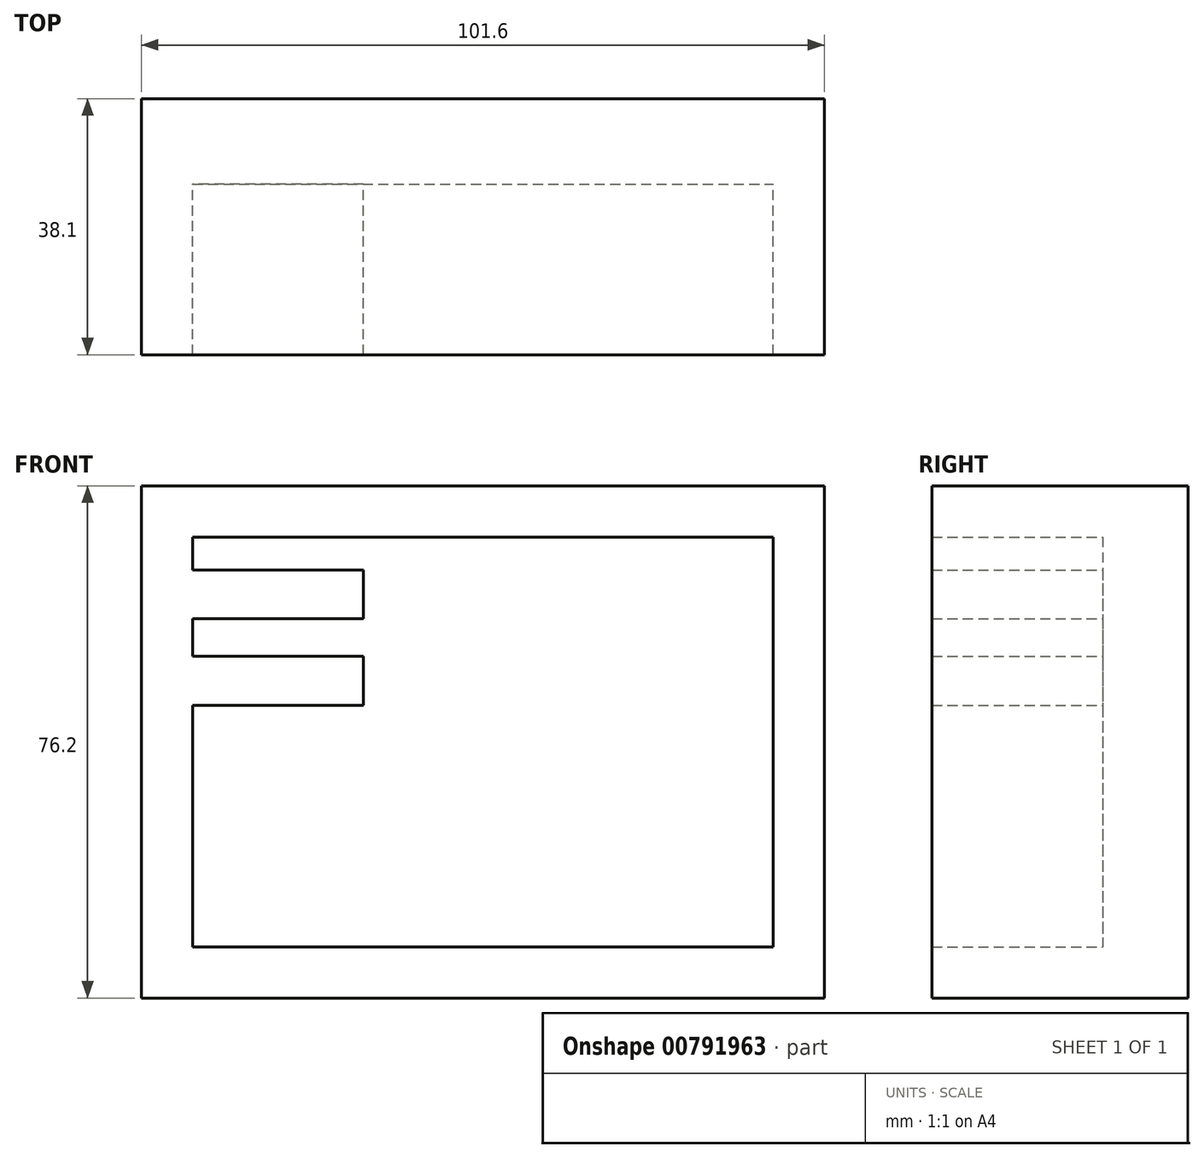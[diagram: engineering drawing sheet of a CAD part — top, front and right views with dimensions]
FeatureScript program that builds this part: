
annotation { "Feature Type Name" : "Feature", "Feature Type Description" : "" }
export const myFeature = defineFeature(function(context is Context, id is Id, definition is map)
    precondition{}
    {
        {
            var Q0;
            Q0=qCreatedBy(makeId("Front.planeOp"),FACE);
            var sketch = newSketch(context, id + "F0", { "sketchPlane" : qUnion([Q0])});
            skLineSegment(sketch, "E0.bottom", {"start": v(-69.79, 37.31) * mm, "end": v(31.81, 37.31) * mm});
            skLineSegment(sketch, "E0.top", {"start": v(-69.79, -38.89) * mm, "end": v(31.81, -38.89) * mm});
            skLineSegment(sketch, "E0.left", {"start": v(-69.79, 37.31) * mm, "end": v(-69.79, -38.89) * mm});
            skLineSegment(sketch, "E0.right", {"start": v(31.81, 37.31) * mm, "end": v(31.81, -38.89) * mm});
            skLineSegment(sketch, "E1.bottom", {"start": v(-62.17, 29.7) * mm, "end": v(24.2, 29.7) * mm});
            skLineSegment(sketch, "E1.top", {"start": v(-62.17, -31.27) * mm, "end": v(24.2, -31.27) * mm});
            skLineSegment(sketch, "E1.left", {"start": v(-62.17, 29.7) * mm, "end": v(-62.17, -31.27) * mm});
            skLineSegment(sketch, "E1.right", {"start": v(24.2, 29.7) * mm, "end": v(24.2, -31.27) * mm});
            skSolve(sketch);
        }
        {
            var Q0;
            Q0=makeQuery(id+"F0.imprint","IMPRINT",FACE,{"disambiguationData":[TD([[makeQuery(id+"F0.imprint","IMPRINT",EDGE,{"derivedFrom":sQuery(id+"F0.wireOp",EDGE,"E0.bottom")}),-1.0]])]});
            extrude(context, id + "F1", {"entities" : qUnion([Q0]), "depth" : 38.1 * mm, "offsetDistance" : 25.4 * mm});
        }
        {
            var Q0;
            Q0=makeQuery(id+"F0.imprint","IMPRINT",FACE,{"disambiguationData":[TD([[makeQuery(id+"F0.imprint","IMPRINT",EDGE,{"derivedFrom":sQuery(id+"F0.wireOp",EDGE,"E1.bottom")}),-1.0]])]});
            extrude(context, id + "F2", {"entities" : qUnion([Q0]), "operationType" : NewBodyOperationType.ADD, "depth" : 12.7 * mm, "offsetDistance" : 25.4 * mm});
        }
        {
            var Q0;
            Q0=makeQuery(id+"F1.opExtrude","SWEPT_FACE",FACE,{"disambiguationData":[OSD([sQuery(id+"F0.wireOp",EDGE,"E1.left")])]});
            var sketch = newSketch(context, id + "F3", { "sketchPlane" : qUnion([Q0])});
            skLineSegment(sketch, "E2.bottom", {"start": v(-38.1, 24.78) * mm, "end": v(-12.7, 24.78) * mm});
            skLineSegment(sketch, "E2.top", {"start": v(-38.1, 17.52) * mm, "end": v(-12.7, 17.52) * mm});
            skLineSegment(sketch, "E2.left", {"start": v(-38.1, 24.78) * mm, "end": v(-38.1, 17.52) * mm});
            skLineSegment(sketch, "E2.right", {"start": v(-12.7, 24.78) * mm, "end": v(-12.7, 17.52) * mm});
            skLineSegment(sketch, "E3.bottom", {"start": v(-38.1, 12.51) * mm, "end": v(-12.7, 12.51) * mm});
            skLineSegment(sketch, "E3.top", {"start": v(-38.1, 5.2) * mm, "end": v(-12.7, 5.2) * mm});
            skLineSegment(sketch, "E3.left", {"start": v(-38.1, 12.51) * mm, "end": v(-38.1, 5.2) * mm});
            skLineSegment(sketch, "E3.right", {"start": v(-12.7, 12.51) * mm, "end": v(-12.7, 5.2) * mm});
            skSolve(sketch);
        }
        {
            var Q0;
            Q0=makeQuery(id+"F3.imprint","IMPRINT",FACE,{"disambiguationData":[TD([[makeQuery(id+"F3.imprint","IMPRINT",EDGE,{"derivedFrom":sQuery(id+"F3.wireOp",EDGE,"E2.bottom")}),-1.0]])]});
            extrude(context, id + "F4", {"entities" : qUnion([Q0]), "operationType" : NewBodyOperationType.ADD, "depth" : 25.4 * mm, "offsetDistance" : 25.4 * mm});
        }
        {
            var Q0;
            {var subQ1=sQuery(id+"F0.wireOp",EDGE,"E1.left");var subQ2=sQuery(id+"F0.wireOp",EDGE,"E1.top");Q0=makeQuery(id+"F4.boolean.opBoolean","SPLIT",FACE,{"disambiguationData":[TD([makeQuery(id+"F1.opExtrude","SWEPT_FACE",FACE,{"disambiguationData":[OSD([subQ2])]})])],"derivedFrom":makeQuery(id+"F1.opExtrude","SWEPT_FACE",FACE,{"disambiguationData":[OSD([subQ1])]})});}
            var sketch = newSketch(context, id + "F5", { "sketchPlane" : qUnion([Q0])});
            skLineSegment(sketch, "E4.bottom", {"start": v(-38.1, 11.95) * mm, "end": v(-12.7, 11.95) * mm});
            skLineSegment(sketch, "E4.top", {"start": v(-38.1, 4.62) * mm, "end": v(-12.7, 4.62) * mm});
            skLineSegment(sketch, "E4.left", {"start": v(-38.1, 11.95) * mm, "end": v(-38.1, 4.62) * mm});
            skLineSegment(sketch, "E4.right", {"start": v(-12.7, 11.95) * mm, "end": v(-12.7, 4.62) * mm});
            skSolve(sketch);
        }
        {
            var Q0;
            Q0=makeQuery(id+"F5.imprint","IMPRINT",FACE,{"disambiguationData":[TD([[makeQuery(id+"F5.imprint","IMPRINT",EDGE,{"derivedFrom":sQuery(id+"F5.wireOp",EDGE,"E4.bottom")}),-1.0]])]});
            extrude(context, id + "F6", {"entities" : qUnion([Q0]), "operationType" : NewBodyOperationType.ADD, "depth" : 25.4 * mm, "offsetDistance" : 25.4 * mm});
        }
    });
